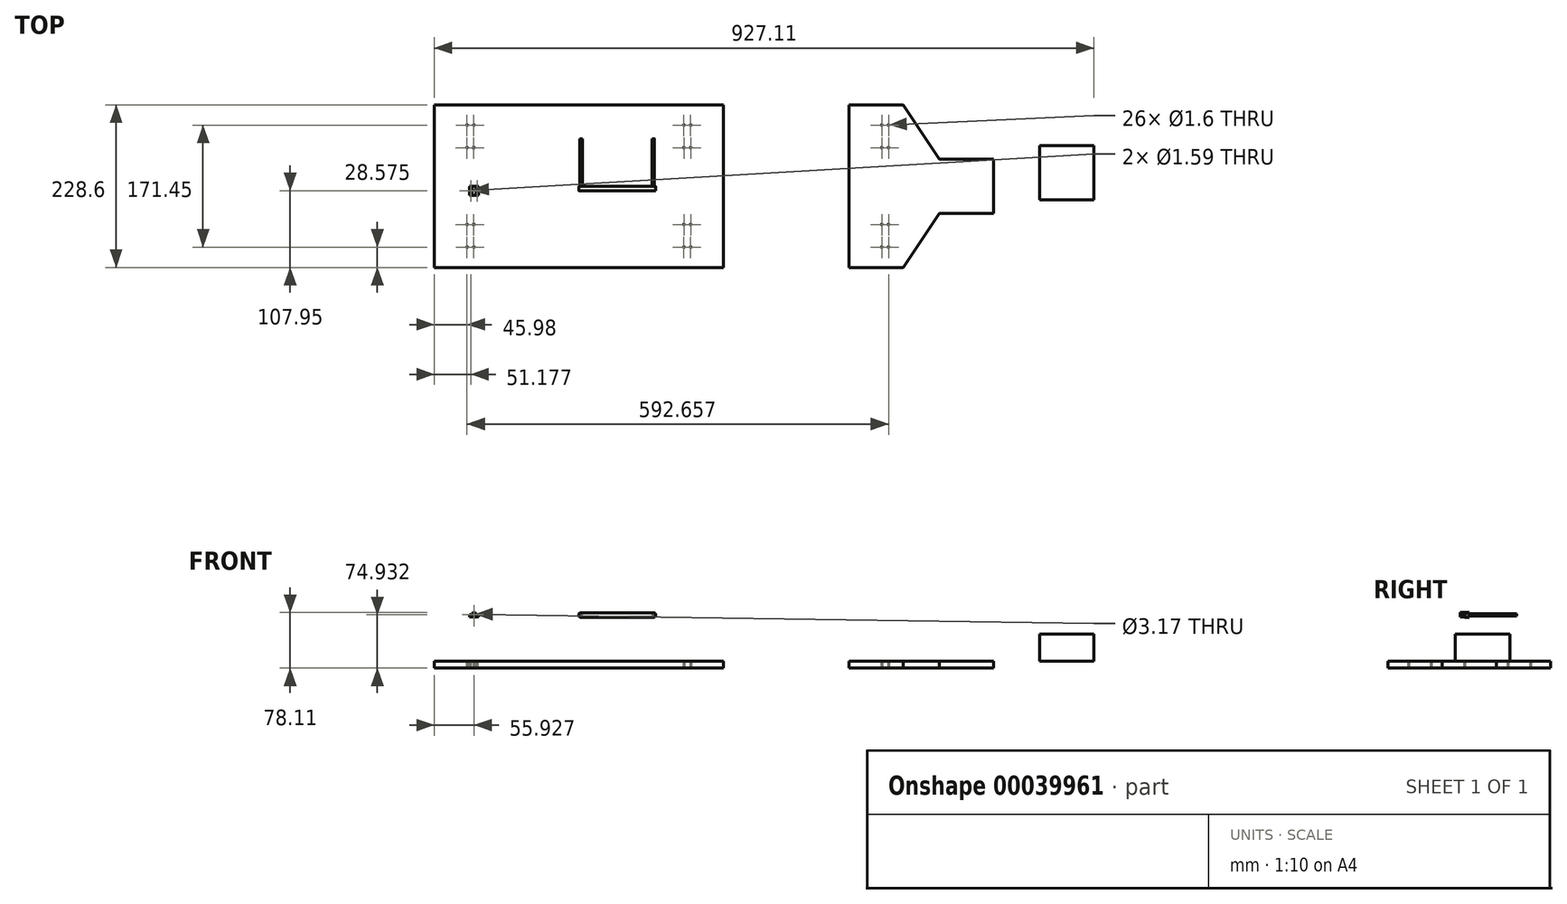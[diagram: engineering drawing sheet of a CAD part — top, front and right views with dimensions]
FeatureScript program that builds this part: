
annotation { "Feature Type Name" : "Feature", "Feature Type Description" : "" }
export const myFeature = defineFeature(function(context is Context, id is Id, definition is map)
    precondition{}
    {
        {
            var Q0;
            Q0=qCreatedBy(makeId("Top.planeOp"),FACE);
            var sketch = newSketch(context, id + "F0", { "sketchPlane" : qUnion([Q0])});
            skLineSegment(sketch, "E0.rect.bottom", {"start": v(203.2, -114.3) * mm, "end": v(-203.2, -114.3) * mm});
            skLineSegment(sketch, "E0.rect.top", {"start": v(203.2, 114.3) * mm, "end": v(-203.2, 114.3) * mm});
            skLineSegment(sketch, "E0.rect.left", {"start": v(203.2, -114.3) * mm, "end": v(203.2, 114.3) * mm});
            skLineSegment(sketch, "E0.rect.right", {"start": v(-203.2, -114.3) * mm, "end": v(-203.2, 114.3) * mm});
            skPoint(sketch, "E0.rect.middle", {"position": v(0, 0) * mm});
            skSolve(sketch);
        }
        {
            var Q0;
            Q0=makeQuery(id+"F0.imprint","IMPRINT",FACE,{"disambiguationData":[TD([[makeQuery(id+"F0.imprint","IMPRINT",EDGE,{"derivedFrom":sQuery(id+"F0.wireOp",EDGE,"E0.rect.bottom")}),-1.0]])]});
            extrude(context, id + "F1", {"entities" : qUnion([Q0]), "oppositeDirection" : true, "depth" : 9.52 * mm});
        }
        {
            var Q0;
            Q0=qCreatedBy(makeId("Top.planeOp"),FACE);
            var sketch = newSketch(context, id + "F2", { "sketchPlane" : qUnion([Q0])});
            skLineSegment(sketch, "E1.rect.right", {"start": v(379.89, -114.3) * mm, "end": v(379.89, 114.3) * mm});
            skLineSegment(sketch, "E2", {"start": v(379.89, 0) * mm, "end": v(583.09, 0) * mm, "construction": true});
            skLineSegment(sketch, "E3.bottom", {"start": v(506.89, 38.1) * mm, "end": v(583.09, 38.1) * mm});
            skLineSegment(sketch, "E3.top", {"start": v(506.89, -38.1) * mm, "end": v(583.09, -38.1) * mm});
            skLineSegment(sketch, "E3.right", {"start": v(583.09, 38.1) * mm, "end": v(583.09, -38.1) * mm});
            skLineSegment(sketch, "E4", {"start": v(379.89, 114.3) * mm, "end": v(456.09, 114.3) * mm});
            skLineSegment(sketch, "E5", {"start": v(456.09, 114.3) * mm, "end": v(506.89, 38.1) * mm});
            skLineSegment(sketch, "E6", {"start": v(379.89, -114.3) * mm, "end": v(456.09, -114.3) * mm});
            skLineSegment(sketch, "E7", {"start": v(456.09, -114.3) * mm, "end": v(506.89, -38.1) * mm});
            skSolve(sketch);
        }
        {
            var Q0;
            Q0=makeQuery(id+"F2.imprint","IMPRINT",FACE,{"disambiguationData":[TD([[makeQuery(id+"F2.imprint","IMPRINT",EDGE,{"derivedFrom":sQuery(id+"F2.wireOp",EDGE,"E1.rect.right")}),-1.0]])]});
            extrude(context, id + "F3", {"entities" : qUnion([Q0]), "oppositeDirection" : true, "depth" : 9.52 * mm});
        }
        {
            var Q0;
            Q0=qCreatedBy(makeId("Front.planeOp"),FACE);
            var sketch = newSketch(context, id + "F4", { "sketchPlane" : qUnion([Q0])});
            skLineSegment(sketch, "E8.bottom", {"start": v(2.54, 68.31) * mm, "end": v(105.41, 68.31) * mm});
            skLineSegment(sketch, "E8.top", {"start": v(2.54, 61.96) * mm, "end": v(105.41, 61.96) * mm});
            skLineSegment(sketch, "E8.left", {"start": v(0, 65.77) * mm, "end": v(0, 64.5) * mm});
            skLineSegment(sketch, "E8.right", {"start": v(107.95, 65.77) * mm, "end": v(107.95, 64.5) * mm});
            skCircle(sketch, "E9", {"center": v(3.17, 65.14) * mm, "radius": 1.59 * mm});
            skPoint(sketch, "E10.visualSharp", {"position": v(0, 68.31) * mm});
            skArc(sketch, "E10.filletArc", {"start": v(2.54, 68.31) * mm, "mid": v(0.74, 67.57) * mm, "end": v(0, 65.77) * mm});
            skPoint(sketch, "E11.visualSharp", {"position": v(0, 61.96) * mm});
            skArc(sketch, "E11.filletArc", {"start": v(0, 64.5) * mm, "mid": v(0.74, 62.7) * mm, "end": v(2.54, 61.96) * mm});
            skLineSegment(sketch, "E12", {"start": v(55.25, 68.31) * mm, "end": v(55.25, 61.96) * mm, "construction": true});
            skCircle(sketch, "E13", {"center": v(104.78, 65.14) * mm, "radius": 1.59 * mm});
            skPoint(sketch, "E14.visualSharp", {"position": v(107.95, 68.31) * mm});
            skArc(sketch, "E14.filletArc", {"start": v(107.95, 65.77) * mm, "mid": v(107.2, 67.57) * mm, "end": v(105.41, 68.31) * mm});
            skPoint(sketch, "E15.visualSharp", {"position": v(107.95, 61.96) * mm});
            skArc(sketch, "E15.filletArc", {"start": v(105.41, 61.96) * mm, "mid": v(107.2, 62.7) * mm, "end": v(107.95, 64.5) * mm});
            skSolve(sketch);
        }
        {
            var Q0;
            Q0=makeQuery(id+"F4.imprint","IMPRINT",FACE,{"disambiguationData":[TD([[makeQuery(id+"F4.imprint","IMPRINT",EDGE,{"derivedFrom":sQuery(id+"F4.wireOp",EDGE,"E8.bottom")}),-1.0]])]});
            extrude(context, id + "F5", {"entities" : qUnion([Q0]), "depth" : 6.35 * mm});
        }
        {
            var Q0;
            Q0=makeQuery(id+"F5.opExtrude","CAP_FACE",FACE,{"disambiguationData":[OSD([sQuery(id+"F4.wireOp",EDGE,"E8.bottom"),sQuery(id+"F4.wireOp",EDGE,"E8.top"),sQuery(id+"F4.wireOp",EDGE,"E8.left"),sQuery(id+"F4.wireOp",EDGE,"E8.right"),sQuery(id+"F4.wireOp",EDGE,"E9"),sQuery(id+"F4.wireOp",EDGE,"E10.filletArc"),sQuery(id+"F4.wireOp",EDGE,"E11.filletArc"),sQuery(id+"F4.wireOp",EDGE,"E13"),sQuery(id+"F4.wireOp",EDGE,"E14.filletArc"),sQuery(id+"F4.wireOp",EDGE,"E15.filletArc")])],"isStart":false});
            var sketch = newSketch(context, id + "F6", { "sketchPlane" : qUnion([Q0])});
            skCircle(sketch, "E16", {"center": v(3.17, 65.14) * mm, "radius": 1.64 * mm});
            skCircle(sketch, "E17", {"center": v(104.78, 65.14) * mm, "radius": 1.59 * mm});
            skSolve(sketch);
        }
        {
            var Q0;
            Q0 = qSketchRegion(id + "F6", true);
            extrude(context, id + "F7", {"entities" : qUnion([Q0]), "operationType" : NewBodyOperationType.ADD, "oppositeDirection" : true, "depth" : 73.02 * mm});
        }
        {
            var Q0;
            Q0=qCreatedBy(makeId("Front.planeOp"),FACE);
            var sketch = newSketch(context, id + "F8", { "sketchPlane" : qUnion([Q0])});
            skArc(sketch, "E18", {"start": v(-144.1, 65.4) * mm, "mid": v(-147.27, 68.58) * mm, "end": v(-150.45, 65.4) * mm});
            skLineSegment(sketch, "E19.right", {"start": v(-153.62, 65.4) * mm, "end": v(-153.62, 62.21) * mm});
            skLineSegment(sketch, "E20", {"start": v(-153.62, 65.4) * mm, "end": v(-150.45, 65.4) * mm});
            skLineSegment(sketch, "E21", {"start": v(-140.92, 65.4) * mm, "end": v(-140.92, 62.21) * mm});
            skLineSegment(sketch, "E22.trimOffspring", {"start": v(-144.1, 65.4) * mm, "end": v(-140.92, 65.4) * mm});
            skCircle(sketch, "E23", {"center": v(-147.27, 65.4) * mm, "radius": 1.59 * mm});
            skLineSegment(sketch, "E24", {"start": v(-153.62, 62.21) * mm, "end": v(-140.92, 62.21) * mm});
            skSolve(sketch);
        }
        {
            var Q0;
            Q0=makeQuery(id+"F8.imprint","IMPRINT",FACE,{"disambiguationData":[TD([[makeQuery(id+"F8.imprint","IMPRINT",EDGE,{"derivedFrom":sQuery(id+"F8.wireOp",EDGE,"E18")}),1.0]])]});
            extrude(context, id + "F9", {"entities" : qUnion([Q0]), "depth" : 12.7 * mm});
        }
        {
            var Q0;
            Q0=makeQuery(id+"F9.opExtrude","SWEPT_FACE",FACE,{"disambiguationData":[OSD([sQuery(id+"F8.wireOp",EDGE,"E20")])]});
            var sketch = newSketch(context, id + "F10", { "sketchPlane" : qUnion([Q0])});
            skCircle(sketch, "E25", {"center": v(-152.02, -6.35) * mm, "radius": 0.8 * mm});
            skCircle(sketch, "E26", {"center": v(-142.52, -6.35) * mm, "radius": 0.8 * mm});
            skSolve(sketch);
        }
        {
            var Q0;
            Q0=makeQuery(id+"F10.imprint","IMPRINT",FACE,{"disambiguationData":[TD([[makeQuery(id+"F10.imprint","IMPRINT",EDGE,{"derivedFrom":sQuery(id+"F10.wireOp",EDGE,"E25")}),1.0]])]});
            var Q1;
            Q1=makeQuery(id+"F10.imprint","IMPRINT",FACE,{"disambiguationData":[TD([[makeQuery(id+"F10.imprint","IMPRINT",EDGE,{"derivedFrom":sQuery(id+"F10.wireOp",EDGE,"E26")}),1.0]])]});
            extrude(context, id + "F11", {"entities" : qUnion([Q0, Q1]), "operationType" : NewBodyOperationType.REMOVE, "endBound" : BoundingType.THROUGH_ALL, "oppositeDirection" : true, "depth" : 25.4 * mm});
        }
        {
            var Q0;
            Q0=makeQuery(id+"F1.opExtrude","CAP_FACE",FACE,{"disambiguationData":[OSD([sQuery(id+"F0.wireOp",EDGE,"E0.rect.bottom"),sQuery(id+"F0.wireOp",EDGE,"E0.rect.top"),sQuery(id+"F0.wireOp",EDGE,"E0.rect.left"),sQuery(id+"F0.wireOp",EDGE,"E0.rect.right")])],"isStart":false});
            var sketch = newSketch(context, id + "F12", { "sketchPlane" : qUnion([Q0])});
            skCircle(sketch, "E27", {"center": v(157.15, 85.73) * mm, "radius": 0.8 * mm});
            skCircle(sketch, "E28", {"center": v(147.65, 85.73) * mm, "radius": 0.8 * mm});
            skLineSegment(sketch, "E29", {"start": v(147.65, 85.73) * mm, "end": v(157.15, 85.73) * mm, "construction": true});
            skPoint(sketch, "E30", {"position": v(152.4, 85.73) * mm});
            skLineSegment(sketch, "E31", {"start": v(0, 114.3) * mm, "end": v(0, -114.3) * mm, "construction": true});
            skLineSegment(sketch, "E32", {"start": v(203.2, 0) * mm, "end": v(-203.2, 0) * mm, "construction": true});
            skCircle(sketch, "E33.MirrorC", {"center": v(-147.65, 85.73) * mm, "radius": 0.8 * mm});
            skCircle(sketch, "E34.MirrorC", {"center": v(-157.15, 85.73) * mm, "radius": 0.8 * mm});
            skCircle(sketch, "E35.MirrorC", {"center": v(147.65, -85.73) * mm, "radius": 0.8 * mm});
            skCircle(sketch, "E36.MirrorC", {"center": v(157.15, -85.73) * mm, "radius": 0.8 * mm});
            skCircle(sketch, "E37.MirrorC", {"center": v(-147.65, -85.73) * mm, "radius": 0.8 * mm});
            skCircle(sketch, "E38.MirrorC", {"center": v(-157.15, -85.73) * mm, "radius": 0.8 * mm});
            skLineSegment(sketch, "E39", {"start": v(152.4, 85.73) * mm, "end": v(152.4, 53.97) * mm, "construction": true});
            skLineSegment(sketch, "E40", {"start": v(147.72, 53.97) * mm, "end": v(157.22, 53.98) * mm, "construction": true});
            skCircle(sketch, "E41", {"center": v(147.72, 53.97) * mm, "radius": 0.8 * mm});
            skCircle(sketch, "E42", {"center": v(157.22, 53.97) * mm, "radius": 0.8 * mm});
            skCircle(sketch, "E43.MirrorC", {"center": v(147.72, -53.98) * mm, "radius": 0.8 * mm});
            skCircle(sketch, "E44.MirrorC", {"center": v(157.22, -53.98) * mm, "radius": 0.8 * mm});
            skCircle(sketch, "E45.MirrorC", {"center": v(-147.72, -53.97) * mm, "radius": 0.8 * mm});
            skCircle(sketch, "E46.MirrorC", {"center": v(-157.22, -53.97) * mm, "radius": 0.8 * mm});
            skCircle(sketch, "E47.MirrorC", {"center": v(-147.72, 53.98) * mm, "radius": 0.8 * mm});
            skCircle(sketch, "E48.MirrorC", {"center": v(-157.22, 53.98) * mm, "radius": 0.8 * mm});
            skSolve(sketch);
        }
        {
            var Q0;
            Q0 = qSketchRegion(id + "F12", true);
            extrude(context, id + "F13", {"entities" : qUnion([Q0]), "operationType" : NewBodyOperationType.REMOVE, "endBound" : BoundingType.THROUGH_ALL, "oppositeDirection" : true, "depth" : 25.4 * mm});
        }
        {
            var Q0;
            Q0=makeQuery(id+"F3.opExtrude","CAP_FACE",FACE,{"disambiguationData":[OSD([sQuery(id+"F2.wireOp",EDGE,"E1.rect.right"),sQuery(id+"F2.wireOp",EDGE,"E3.bottom"),sQuery(id+"F2.wireOp",EDGE,"E3.top"),sQuery(id+"F2.wireOp",EDGE,"E3.right"),sQuery(id+"F2.wireOp",EDGE,"E4"),sQuery(id+"F2.wireOp",EDGE,"E5"),sQuery(id+"F2.wireOp",EDGE,"E6"),sQuery(id+"F2.wireOp",EDGE,"E7")])],"isStart":false});
            var sketch = newSketch(context, id + "F14", { "sketchPlane" : qUnion([Q0])});
            skCircle(sketch, "E49", {"center": v(425.94, 85.73) * mm, "radius": 0.8 * mm});
            skCircle(sketch, "E50", {"center": v(435.44, 85.73) * mm, "radius": 0.8 * mm});
            skLineSegment(sketch, "E51", {"start": v(425.94, 85.73) * mm, "end": v(435.44, 85.73) * mm, "construction": true});
            skPoint(sketch, "E52", {"position": v(430.69, 85.73) * mm});
            skLineSegment(sketch, "E53", {"start": v(379.89, 0) * mm, "end": v(583.09, 0) * mm, "construction": true});
            skCircle(sketch, "E54.MirrorC", {"center": v(425.94, -85.73) * mm, "radius": 0.8 * mm});
            skCircle(sketch, "E55.MirrorC", {"center": v(435.44, -85.73) * mm, "radius": 0.8 * mm});
            skLineSegment(sketch, "E56", {"start": v(430.69, 85.73) * mm, "end": v(430.69, 53.98) * mm, "construction": true});
            skLineSegment(sketch, "E57", {"start": v(425.94, 53.98) * mm, "end": v(435.44, 53.98) * mm, "construction": true});
            skCircle(sketch, "E58", {"center": v(425.94, 53.98) * mm, "radius": 0.8 * mm});
            skCircle(sketch, "E59", {"center": v(435.44, 53.98) * mm, "radius": 0.8 * mm});
            skCircle(sketch, "E60.MirrorC", {"center": v(435.44, -53.98) * mm, "radius": 0.8 * mm});
            skCircle(sketch, "E61.MirrorC", {"center": v(425.94, -53.98) * mm, "radius": 0.8 * mm});
            skSolve(sketch);
        }
        {
            var Q0;
            Q0 = qSketchRegion(id + "F14", true);
            extrude(context, id + "F15", {"entities" : qUnion([Q0]), "operationType" : NewBodyOperationType.REMOVE, "endBound" : BoundingType.THROUGH_ALL, "oppositeDirection" : true, "depth" : 25.4 * mm});
        }
        {
            var Q0;
            Q0=qCreatedBy(makeId("Top.planeOp"),FACE);
            var sketch = newSketch(context, id + "F16", { "sketchPlane" : qUnion([Q0])});
            skLineSegment(sketch, "E62.bottom", {"start": v(647.7, 56.64) * mm, "end": v(723.9, 56.64) * mm});
            skLineSegment(sketch, "E62.top", {"start": v(647.7, -19.56) * mm, "end": v(723.9, -19.56) * mm});
            skLineSegment(sketch, "E62.left", {"start": v(647.7, 56.64) * mm, "end": v(647.7, -19.56) * mm});
            skLineSegment(sketch, "E62.right", {"start": v(723.9, 56.64) * mm, "end": v(723.9, -19.56) * mm});
            skSolve(sketch);
        }
        {
            var Q0;
            Q0=makeQuery(id+"F16.imprint","IMPRINT",FACE,{"disambiguationData":[TD([[makeQuery(id+"F16.imprint","IMPRINT",EDGE,{"derivedFrom":sQuery(id+"F16.wireOp",EDGE,"E62.bottom")}),-1.0]])]});
            extrude(context, id + "F17", {"entities" : qUnion([Q0]), "depth" : 38.1 * mm});
        }
    });
